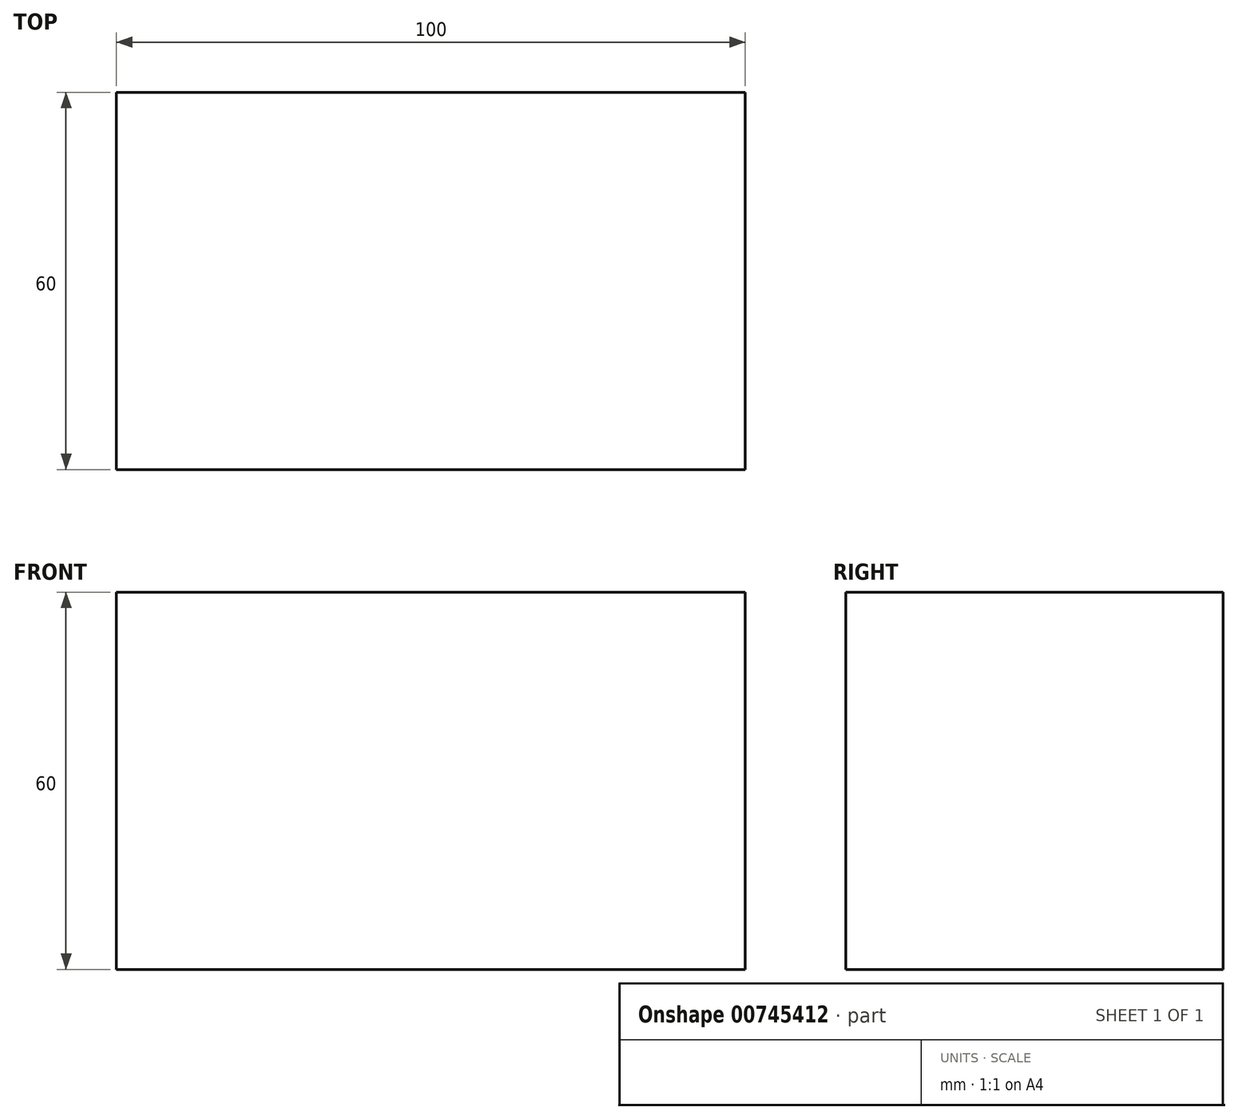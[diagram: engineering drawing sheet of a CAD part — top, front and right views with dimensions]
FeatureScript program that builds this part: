
annotation { "Feature Type Name" : "Feature", "Feature Type Description" : "" }
export const myFeature = defineFeature(function(context is Context, id is Id, definition is map)
    precondition{}
    {
        {
            var Q0;
            Q0=qCreatedBy(makeId("Front.planeOp"),FACE);
            var sketch = newSketch(context, id + "F0", { "sketchPlane" : qUnion([Q0])});
            skLineSegment(sketch, "E0.bottom", {"start": v(-50, -30) * mm, "end": v(50, -30) * mm});
            skLineSegment(sketch, "E0.top", {"start": v(-50, 30) * mm, "end": v(50, 30) * mm});
            skLineSegment(sketch, "E0.left", {"start": v(-50, -30) * mm, "end": v(-50, 30) * mm});
            skLineSegment(sketch, "E0.right", {"start": v(50, -30) * mm, "end": v(50, 30) * mm});
            skPoint(sketch, "E0.middle", {"position": v(0, 0) * mm});
            skSolve(sketch);
        }
        {
            var Q0;
            Q0=makeQuery(id+"F0.imprint","IMPRINT",FACE,{"disambiguationData":[TD([[makeQuery(id+"F0.imprint","IMPRINT",EDGE,{"derivedFrom":sQuery(id+"F0.wireOp",EDGE,"E0.bottom")}),1.0]])]});
            extrude(context, id + "F1", {"entities" : qUnion([Q0]), "depth" : 60 * mm, "offsetDistance" : 25 * mm});
        }
    });
